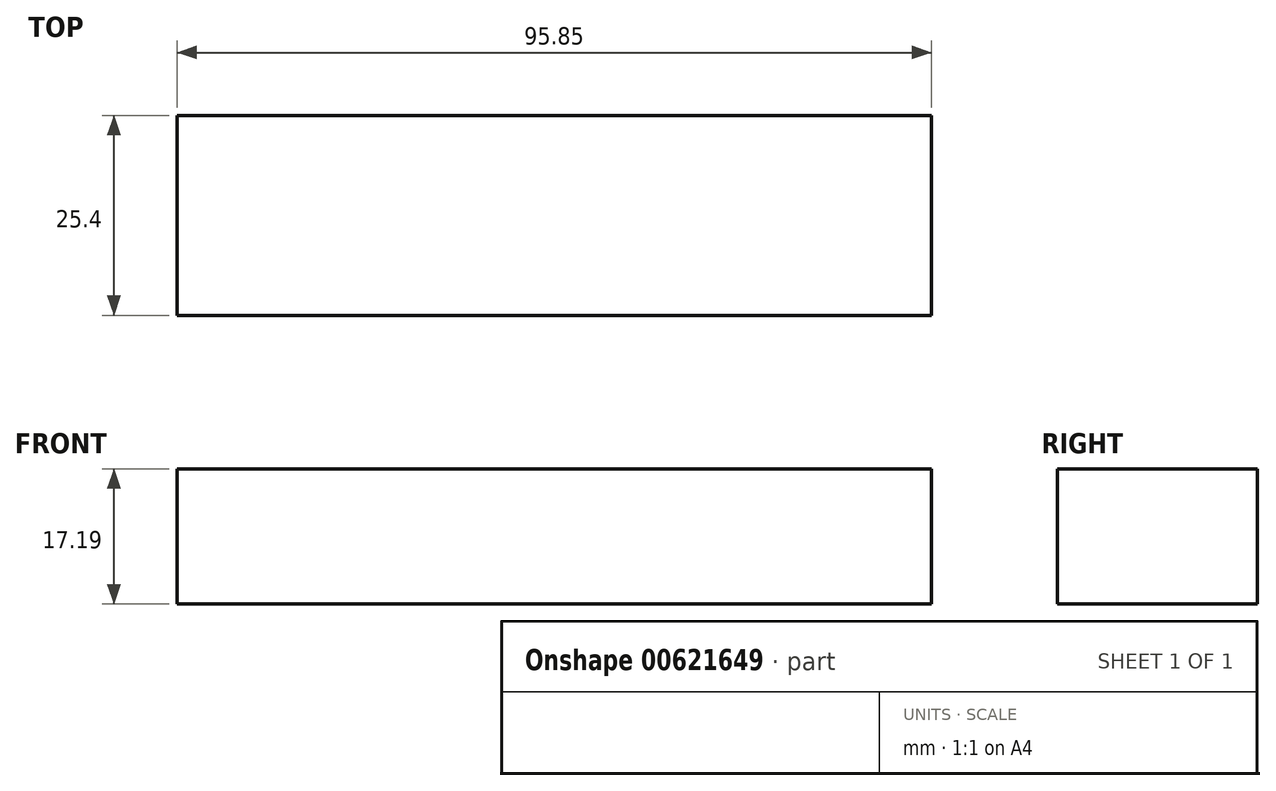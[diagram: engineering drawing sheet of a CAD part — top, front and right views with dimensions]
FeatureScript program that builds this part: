
annotation { "Feature Type Name" : "Feature", "Feature Type Description" : "" }
export const myFeature = defineFeature(function(context is Context, id is Id, definition is map)
    precondition{}
    {
        {
            var Q0;
            Q0=qCreatedBy(makeId("Front.planeOp"),FACE);
            var sketch = newSketch(context, id + "F0", { "sketchPlane" : qUnion([Q0])});
            skLineSegment(sketch, "E0.bottom", {"start": v(-68.87, -10.87) * mm, "end": v(26.98, -10.87) * mm});
            skLineSegment(sketch, "E0.top", {"start": v(-68.87, -28.06) * mm, "end": v(26.98, -28.06) * mm});
            skLineSegment(sketch, "E0.left", {"start": v(-68.87, -10.87) * mm, "end": v(-68.87, -28.06) * mm});
            skLineSegment(sketch, "E0.right", {"start": v(26.98, -10.87) * mm, "end": v(26.98, -28.06) * mm});
            skLineSegment(sketch, "E1.bottom", {"start": v(98.13, 55.44) * mm, "end": v(64.3, 55.44) * mm});
            skLineSegment(sketch, "E1.top", {"start": v(98.13, 27.79) * mm, "end": v(64.3, 27.79) * mm});
            skLineSegment(sketch, "E1.left", {"start": v(98.13, 55.44) * mm, "end": v(98.13, 27.79) * mm});
            skLineSegment(sketch, "E1.right", {"start": v(64.3, 55.44) * mm, "end": v(64.3, 27.79) * mm});
            skFitSpline(sketch, "E2", {"points": [v(26.98, -10.87) * mm, v(19.47, 25.1) * mm, v(64.3, 27.79) * mm], "startDerivative": vector(-39.87, 92.53) * mm, "endDerivative": vector(111.97, -13.43) * mm});
            skPoint(sketch, "E3.1.internal.snap0", {"position": v(-20.94, -10.87) * mm});
            skFitSpline(sketch, "E3", {"points": [v(-7.65, -10.87) * mm, v(-20.94, 34.5) * mm, v(64.3, 55.44) * mm], "startDerivative": vector(-69.33, 122.2) * mm, "endDerivative": vector(199.49, 15.87) * mm});
            skLineSegment(sketch, "E4.bottom", {"start": v(-68.87, -10.87) * mm, "end": v(-48.2, -10.87) * mm});
            skLineSegment(sketch, "E4.top", {"start": v(-68.87, 43.63) * mm, "end": v(-48.2, 43.63) * mm});
            skLineSegment(sketch, "E4.left", {"start": v(-68.87, -10.87) * mm, "end": v(-68.87, 43.63) * mm});
            skLineSegment(sketch, "E4.right", {"start": v(-48.2, -10.87) * mm, "end": v(-48.2, 43.63) * mm});
            skLineSegment(sketch, "E5.bottom", {"start": v(-48.2, 43.63) * mm, "end": v(-27.52, 43.63) * mm});
            skLineSegment(sketch, "E5.top", {"start": v(-48.2, -10.87) * mm, "end": v(-27.52, -10.87) * mm});
            skLineSegment(sketch, "E5.left", {"start": v(-48.2, 43.63) * mm, "end": v(-48.2, -10.87) * mm});
            skLineSegment(sketch, "E5.right", {"start": v(-27.52, 43.63) * mm, "end": v(-27.52, -10.87) * mm});
            skLineSegment(sketch, "E6.top", {"start": v(-48.2, 63.5) * mm, "end": v(-27.52, 63.5) * mm});
            skLineSegment(sketch, "E6.left", {"start": v(-48.2, 43.63) * mm, "end": v(-48.2, 63.5) * mm});
            skLineSegment(sketch, "E6.right", {"start": v(-27.52, 43.63) * mm, "end": v(-27.52, 63.5) * mm});
            skSolve(sketch);
        }
        {
            var Q0;
            Q0=makeQuery(id+"F0.imprint","IMPRINT",FACE,{"disambiguationData":[TD([[makeQuery(id+"F0.imprint","IMPRINT",EDGE,{"derivedFrom":sQuery(id+"F0.wireOp",EDGE,"E0.bottom")}),-1.0]])]});
            extrude(context, id + "F1", {"entities" : qUnion([Q0]), "depth" : 25.4 * mm, "offsetDistance" : 25.4 * mm});
        }
    });
